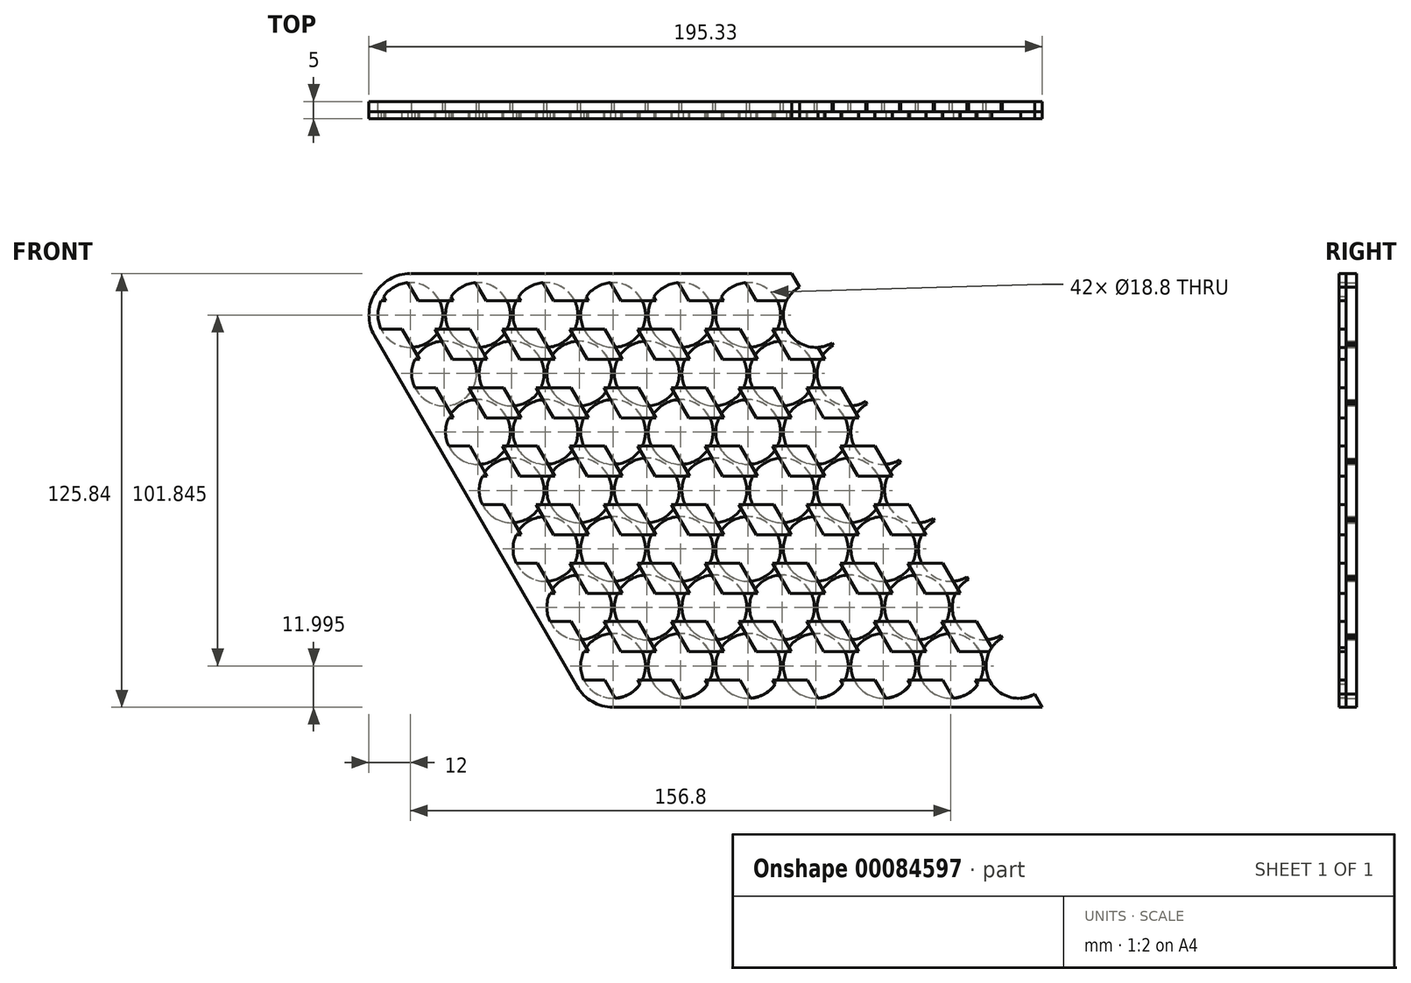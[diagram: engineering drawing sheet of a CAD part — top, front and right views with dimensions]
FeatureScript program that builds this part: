
annotation { "Feature Type Name" : "Feature", "Feature Type Description" : "" }
export const myFeature = defineFeature(function(context is Context, id is Id, definition is map)
    precondition{}
    {
        {
            var Q0;
            Q0=qCreatedBy(makeId("Front.planeOp"),FACE);
            var sketch = newSketch(context, id + "F0", { "sketchPlane" : qUnion([Q0]) });
            skLineSegment(sketch, "E0", {"start": v(0, 0) * mm, "end": v(79.44, 0) * mm, "construction": true});
            skLineSegment(sketch, "E1", {"start": v(0, 0) * mm, "end": v(43.4, -75.16) * mm, "construction": true});
            skCircle(sketch, "E2", {"center": v(0, 0) * mm, "radius": 9.4 * mm});
            skCircle(sketch, "E3.1.0.0", {"center": v(19.6, 0) * mm, "radius": 9.4 * mm});
            skCircle(sketch, "E3.2.0.0", {"center": v(39.2, 0) * mm, "radius": 9.4 * mm});
            skCircle(sketch, "E3.3.0.0", {"center": v(58.8, 0) * mm, "radius": 9.4 * mm});
            skCircle(sketch, "E3.4.0.0", {"center": v(78.4, 0) * mm, "radius": 9.4 * mm});
            skCircle(sketch, "E3.5.0.0", {"center": v(98, 0) * mm, "radius": 9.4 * mm});
            skArc(sketch, "E3.6.0.0", {"start": v(112.9, 8.14) * mm, "mid": v(109.46, -4.7) * mm, "end": v(122.3, -8.14) * mm});
            skLineSegment(sketch, "E3.direction1", {"start": v(0, 0) * mm, "end": v(19.6, 0) * mm, "construction": true});
            skCircle(sketch, "E4.1.0.0", {"center": v(9.8, -16.97) * mm, "radius": 9.4 * mm});
            skCircle(sketch, "E4.2.0.0", {"center": v(19.6, -33.95) * mm, "radius": 9.4 * mm});
            skCircle(sketch, "E4.3.0.0", {"center": v(29.4, -50.92) * mm, "radius": 9.4 * mm});
            skCircle(sketch, "E4.4.0.0", {"center": v(39.2, -67.9) * mm, "radius": 9.4 * mm});
            skCircle(sketch, "E4.5.0.0", {"center": v(49, -84.87) * mm, "radius": 9.4 * mm});
            skCircle(sketch, "E4.6.0.0", {"center": v(58.8, -101.84) * mm, "radius": 9.4 * mm});
            skLineSegment(sketch, "E4.direction1", {"start": v(0, 0) * mm, "end": v(9.8, -16.97) * mm, "construction": true});
            skCircle(sketch, "E5.1.0.0", {"center": v(29.4, -16.97) * mm, "radius": 9.4 * mm});
            skCircle(sketch, "E5.1.0.1", {"center": v(39.2, -33.95) * mm, "radius": 9.4 * mm});
            skCircle(sketch, "E5.1.0.2", {"center": v(49, -50.92) * mm, "radius": 9.4 * mm});
            skCircle(sketch, "E5.1.0.3", {"center": v(58.8, -67.9) * mm, "radius": 9.4 * mm});
            skCircle(sketch, "E5.1.0.4", {"center": v(68.6, -84.87) * mm, "radius": 9.4 * mm});
            skCircle(sketch, "E5.1.0.5", {"center": v(78.4, -101.84) * mm, "radius": 9.4 * mm});
            skCircle(sketch, "E5.2.0.0", {"center": v(49, -16.97) * mm, "radius": 9.4 * mm});
            skCircle(sketch, "E5.2.0.1", {"center": v(58.8, -33.95) * mm, "radius": 9.4 * mm});
            skCircle(sketch, "E5.2.0.2", {"center": v(68.6, -50.92) * mm, "radius": 9.4 * mm});
            skCircle(sketch, "E5.2.0.3", {"center": v(78.4, -67.9) * mm, "radius": 9.4 * mm});
            skCircle(sketch, "E5.2.0.4", {"center": v(88.2, -84.87) * mm, "radius": 9.4 * mm});
            skCircle(sketch, "E5.2.0.5", {"center": v(98, -101.84) * mm, "radius": 9.4 * mm});
            skCircle(sketch, "E5.3.0.0", {"center": v(68.6, -16.97) * mm, "radius": 9.4 * mm});
            skCircle(sketch, "E5.3.0.1", {"center": v(78.4, -33.95) * mm, "radius": 9.4 * mm});
            skCircle(sketch, "E5.3.0.2", {"center": v(88.2, -50.92) * mm, "radius": 9.4 * mm});
            skCircle(sketch, "E5.3.0.3", {"center": v(98, -67.9) * mm, "radius": 9.4 * mm});
            skCircle(sketch, "E5.3.0.4", {"center": v(107.8, -84.87) * mm, "radius": 9.4 * mm});
            skCircle(sketch, "E5.3.0.5", {"center": v(117.6, -101.84) * mm, "radius": 9.4 * mm});
            skCircle(sketch, "E5.4.0.0", {"center": v(88.2, -16.97) * mm, "radius": 9.4 * mm});
            skCircle(sketch, "E5.4.0.1", {"center": v(98, -33.95) * mm, "radius": 9.4 * mm});
            skCircle(sketch, "E5.4.0.2", {"center": v(107.8, -50.92) * mm, "radius": 9.4 * mm});
            skCircle(sketch, "E5.4.0.3", {"center": v(117.6, -67.9) * mm, "radius": 9.4 * mm});
            skCircle(sketch, "E5.4.0.4", {"center": v(127.4, -84.87) * mm, "radius": 9.4 * mm});
            skCircle(sketch, "E5.4.0.5", {"center": v(137.2, -101.84) * mm, "radius": 9.4 * mm});
            skCircle(sketch, "E5.5.0.0", {"center": v(107.8, -16.97) * mm, "radius": 9.4 * mm});
            skCircle(sketch, "E5.5.0.1", {"center": v(117.6, -33.95) * mm, "radius": 9.4 * mm});
            skCircle(sketch, "E5.5.0.2", {"center": v(127.4, -50.92) * mm, "radius": 9.4 * mm});
            skCircle(sketch, "E5.5.0.3", {"center": v(137.2, -67.9) * mm, "radius": 9.4 * mm});
            skCircle(sketch, "E5.5.0.4", {"center": v(147, -84.87) * mm, "radius": 9.4 * mm});
            skCircle(sketch, "E5.5.0.5", {"center": v(156.8, -101.84) * mm, "radius": 9.4 * mm});
            skArc(sketch, "E5.6.0.0", {"start": v(122.7, -8.83) * mm, "mid": v(119.26, -21.67) * mm, "end": v(132.1, -25.11) * mm});
            skArc(sketch, "E5.6.0.1", {"start": v(132.5, -25.8) * mm, "mid": v(129.06, -38.65) * mm, "end": v(141.9, -42.09) * mm});
            skArc(sketch, "E5.6.0.2", {"start": v(142.3, -42.78) * mm, "mid": v(138.86, -55.62) * mm, "end": v(151.7, -59.06) * mm});
            skArc(sketch, "E5.6.0.3", {"start": v(152.1, -59.76) * mm, "mid": v(148.66, -72.6) * mm, "end": v(161.5, -76.04) * mm});
            skArc(sketch, "E5.6.0.4", {"start": v(161.9, -76.73) * mm, "mid": v(158.46, -89.57) * mm, "end": v(171.3, -93.01) * mm});
            skArc(sketch, "E5.6.0.5", {"start": v(171.7, -93.7) * mm, "mid": v(168.26, -106.54) * mm, "end": v(181.1, -109.99) * mm});
            skLineSegment(sketch, "E5.direction1", {"start": v(9.8, -16.97) * mm, "end": v(29.4, -16.97) * mm, "construction": true});
            skLineSegment(sketch, "E6", {"start": v(0, 0) * mm, "end": v(127, 0) * mm, "construction": true});
            skLineSegment(sketch, "E7", {"start": v(441, -118.82) * mm, "end": v(68.6, -118.82) * mm, "construction": true});
            skLineSegment(sketch, "E8", {"start": v(68.6, -118.82) * mm, "end": v(0, 0) * mm, "construction": true});
            skArc(sketch, "E9", {"start": v(48.4, -107.84) * mm, "mid": v(52.8, -112.24) * mm, "end": v(58.8, -113.84) * mm});
            skArc(sketch, "E10", {"start": v(0, 12) * mm, "mid": v(-10.4, 6) * mm, "end": v(-10.4, -6) * mm});
            skLineSegment(sketch, "E11", {"start": v(0, 12) * mm, "end": v(110.67, 12) * mm});
            skLineSegment(sketch, "E12", {"start": v(-10.4, -6) * mm, "end": v(48.4, -107.84) * mm});
            skLineSegment(sketch, "E13", {"start": v(58.8, -113.84) * mm, "end": v(183.33, -113.84) * mm});
            skLineSegment(sketch, "E14", {"start": v(117.6, 0) * mm, "end": v(176.4, -101.84) * mm});
            skLineSegment(sketch, "E15", {"start": v(176.4, -101.84) * mm, "end": v(183.33, -113.84) * mm});
            skLineSegment(sketch, "E16", {"start": v(117.6, 0) * mm, "end": v(110.67, 12) * mm});
            skSolve(sketch);
        }
        {
            var Q0;
            Q0=makeQuery(id+"F0.imprint","IMPRINT",FACE,{"disambiguationData":[TD([[makeQuery(id+"F0.imprint","IMPRINT",EDGE,{"derivedFrom":sQuery(id+"F0.wireOp",EDGE,"E2")}),-1.0]])]});
            extrude(context, id + "F1", {"entities" : qUnion([Q0]), "depth" : 3 * mm});
        }
        {
            var Q0;
            Q0=makeQuery(id+"F1.opExtrude","CAP_FACE",FACE,{"disambiguationData":[OSD([sQuery(id+"F0.wireOp",EDGE,"E2"),sQuery(id+"F0.wireOp",EDGE,"E3.1.0.0"),sQuery(id+"F0.wireOp",EDGE,"E3.2.0.0"),sQuery(id+"F0.wireOp",EDGE,"E3.3.0.0"),sQuery(id+"F0.wireOp",EDGE,"E3.4.0.0"),sQuery(id+"F0.wireOp",EDGE,"E3.5.0.0"),sQuery(id+"F0.wireOp",EDGE,"E3.6.0.0"),sQuery(id+"F0.wireOp",EDGE,"E3.7.0.0"),sQuery(id+"F0.wireOp",EDGE,"E3.8.0.0"),sQuery(id+"F0.wireOp",EDGE,"E3.9.0.0"),sQuery(id+"F0.wireOp",EDGE,"E3.10.0.0"),sQuery(id+"F0.wireOp",EDGE,"E3.11.0.0"),sQuery(id+"F0.wireOp",EDGE,"E3.12.0.0"),sQuery(id+"F0.wireOp",EDGE,"E3.13.0.0"),sQuery(id+"F0.wireOp",EDGE,"E3.14.0.0"),sQuery(id+"F0.wireOp",EDGE,"E3.15.0.0"),sQuery(id+"F0.wireOp",EDGE,"E3.16.0.0"),sQuery(id+"F0.wireOp",EDGE,"E3.17.0.0"),sQuery(id+"F0.wireOp",EDGE,"E3.18.0.0"),sQuery(id+"F0.wireOp",EDGE,"E3.19.0.0"),sQuery(id+"F0.wireOp",EDGE,"E4.1.0.0"),sQuery(id+"F0.wireOp",EDGE,"E4.2.0.0"),sQuery(id+"F0.wireOp",EDGE,"E4.3.0.0"),sQuery(id+"F0.wireOp",EDGE,"E4.4.0.0"),sQuery(id+"F0.wireOp",EDGE,"E4.5.0.0"),sQuery(id+"F0.wireOp",EDGE,"E4.6.0.0"),sQuery(id+"F0.wireOp",EDGE,"E5.1.0.0"),sQuery(id+"F0.wireOp",EDGE,"E5.1.0.1"),sQuery(id+"F0.wireOp",EDGE,"E5.1.0.2"),sQuery(id+"F0.wireOp",EDGE,"E5.1.0.3"),sQuery(id+"F0.wireOp",EDGE,"E5.1.0.4"),sQuery(id+"F0.wireOp",EDGE,"E5.1.0.5"),sQuery(id+"F0.wireOp",EDGE,"E5.2.0.0"),sQuery(id+"F0.wireOp",EDGE,"E5.2.0.1"),sQuery(id+"F0.wireOp",EDGE,"E5.2.0.2"),sQuery(id+"F0.wireOp",EDGE,"E5.2.0.3"),sQuery(id+"F0.wireOp",EDGE,"E5.2.0.4"),sQuery(id+"F0.wireOp",EDGE,"E5.2.0.5"),sQuery(id+"F0.wireOp",EDGE,"E5.3.0.0"),sQuery(id+"F0.wireOp",EDGE,"E5.3.0.1"),sQuery(id+"F0.wireOp",EDGE,"E5.3.0.2"),sQuery(id+"F0.wireOp",EDGE,"E5.3.0.3"),sQuery(id+"F0.wireOp",EDGE,"E5.3.0.4"),sQuery(id+"F0.wireOp",EDGE,"E5.3.0.5"),sQuery(id+"F0.wireOp",EDGE,"E5.4.0.0"),sQuery(id+"F0.wireOp",EDGE,"E5.4.0.1"),sQuery(id+"F0.wireOp",EDGE,"E5.4.0.2"),sQuery(id+"F0.wireOp",EDGE,"E5.4.0.3"),sQuery(id+"F0.wireOp",EDGE,"E5.4.0.4"),sQuery(id+"F0.wireOp",EDGE,"E5.4.0.5"),sQuery(id+"F0.wireOp",EDGE,"E5.5.0.0"),sQuery(id+"F0.wireOp",EDGE,"E5.5.0.1"),sQuery(id+"F0.wireOp",EDGE,"E5.5.0.2"),sQuery(id+"F0.wireOp",EDGE,"E5.5.0.3"),sQuery(id+"F0.wireOp",EDGE,"E5.5.0.4"),sQuery(id+"F0.wireOp",EDGE,"E5.5.0.5"),sQuery(id+"F0.wireOp",EDGE,"E5.6.0.0"),sQuery(id+"F0.wireOp",EDGE,"E5.6.0.1"),sQuery(id+"F0.wireOp",EDGE,"E5.6.0.2"),sQuery(id+"F0.wireOp",EDGE,"E5.6.0.3"),sQuery(id+"F0.wireOp",EDGE,"E5.6.0.4"),sQuery(id+"F0.wireOp",EDGE,"E5.6.0.5"),sQuery(id+"F0.wireOp",EDGE,"E5.7.0.0"),sQuery(id+"F0.wireOp",EDGE,"E5.7.0.1"),sQuery(id+"F0.wireOp",EDGE,"E5.7.0.2"),sQuery(id+"F0.wireOp",EDGE,"E5.7.0.3"),sQuery(id+"F0.wireOp",EDGE,"E5.7.0.4"),sQuery(id+"F0.wireOp",EDGE,"E5.7.0.5"),sQuery(id+"F0.wireOp",EDGE,"E5.8.0.0"),sQuery(id+"F0.wireOp",EDGE,"E5.8.0.1"),sQuery(id+"F0.wireOp",EDGE,"E5.8.0.2"),sQuery(id+"F0.wireOp",EDGE,"E5.8.0.3"),sQuery(id+"F0.wireOp",EDGE,"E5.8.0.4"),sQuery(id+"F0.wireOp",EDGE,"E5.8.0.5"),sQuery(id+"F0.wireOp",EDGE,"E5.9.0.0"),sQuery(id+"F0.wireOp",EDGE,"E5.9.0.1"),sQuery(id+"F0.wireOp",EDGE,"E5.9.0.2"),sQuery(id+"F0.wireOp",EDGE,"E5.9.0.3"),sQuery(id+"F0.wireOp",EDGE,"E5.9.0.4"),sQuery(id+"F0.wireOp",EDGE,"E5.9.0.5"),sQuery(id+"F0.wireOp",EDGE,"E5.10.0.0"),sQuery(id+"F0.wireOp",EDGE,"E5.10.0.1"),sQuery(id+"F0.wireOp",EDGE,"E5.10.0.2"),sQuery(id+"F0.wireOp",EDGE,"E5.10.0.3"),sQuery(id+"F0.wireOp",EDGE,"E5.10.0.4"),sQuery(id+"F0.wireOp",EDGE,"E5.10.0.5"),sQuery(id+"F0.wireOp",EDGE,"E5.11.0.0"),sQuery(id+"F0.wireOp",EDGE,"E5.11.0.1"),sQuery(id+"F0.wireOp",EDGE,"E5.11.0.2"),sQuery(id+"F0.wireOp",EDGE,"E5.11.0.3"),sQuery(id+"F0.wireOp",EDGE,"E5.11.0.4"),sQuery(id+"F0.wireOp",EDGE,"E5.11.0.5"),sQuery(id+"F0.wireOp",EDGE,"E5.12.0.0"),sQuery(id+"F0.wireOp",EDGE,"E5.12.0.1"),sQuery(id+"F0.wireOp",EDGE,"E5.12.0.2"),sQuery(id+"F0.wireOp",EDGE,"E5.12.0.3"),sQuery(id+"F0.wireOp",EDGE,"E5.12.0.4"),sQuery(id+"F0.wireOp",EDGE,"E5.12.0.5"),sQuery(id+"F0.wireOp",EDGE,"E5.13.0.0"),sQuery(id+"F0.wireOp",EDGE,"E5.13.0.1"),sQuery(id+"F0.wireOp",EDGE,"E5.13.0.2"),sQuery(id+"F0.wireOp",EDGE,"E5.13.0.3"),sQuery(id+"F0.wireOp",EDGE,"E5.13.0.4"),sQuery(id+"F0.wireOp",EDGE,"E5.13.0.5"),sQuery(id+"F0.wireOp",EDGE,"E5.14.0.0"),sQuery(id+"F0.wireOp",EDGE,"E5.14.0.1"),sQuery(id+"F0.wireOp",EDGE,"E5.14.0.2"),sQuery(id+"F0.wireOp",EDGE,"E5.14.0.3"),sQuery(id+"F0.wireOp",EDGE,"E5.14.0.4"),sQuery(id+"F0.wireOp",EDGE,"E5.14.0.5"),sQuery(id+"F0.wireOp",EDGE,"E5.15.0.0"),sQuery(id+"F0.wireOp",EDGE,"E5.15.0.1"),sQuery(id+"F0.wireOp",EDGE,"E5.15.0.2"),sQuery(id+"F0.wireOp",EDGE,"E5.15.0.3"),sQuery(id+"F0.wireOp",EDGE,"E5.15.0.4"),sQuery(id+"F0.wireOp",EDGE,"E5.15.0.5"),sQuery(id+"F0.wireOp",EDGE,"E5.16.0.0"),sQuery(id+"F0.wireOp",EDGE,"E5.16.0.1"),sQuery(id+"F0.wireOp",EDGE,"E5.16.0.2"),sQuery(id+"F0.wireOp",EDGE,"E5.16.0.3"),sQuery(id+"F0.wireOp",EDGE,"E5.16.0.4"),sQuery(id+"F0.wireOp",EDGE,"E5.16.0.5"),sQuery(id+"F0.wireOp",EDGE,"E5.17.0.0"),sQuery(id+"F0.wireOp",EDGE,"E5.17.0.1"),sQuery(id+"F0.wireOp",EDGE,"E5.17.0.2"),sQuery(id+"F0.wireOp",EDGE,"E5.17.0.3"),sQuery(id+"F0.wireOp",EDGE,"E5.17.0.4"),sQuery(id+"F0.wireOp",EDGE,"E5.17.0.5"),sQuery(id+"F0.wireOp",EDGE,"E5.18.0.0"),sQuery(id+"F0.wireOp",EDGE,"E5.18.0.1"),sQuery(id+"F0.wireOp",EDGE,"E5.18.0.2"),sQuery(id+"F0.wireOp",EDGE,"E5.18.0.3"),sQuery(id+"F0.wireOp",EDGE,"E5.18.0.4"),sQuery(id+"F0.wireOp",EDGE,"E5.18.0.5"),sQuery(id+"F0.wireOp",EDGE,"E5.19.0.0"),sQuery(id+"F0.wireOp",EDGE,"E5.19.0.1"),sQuery(id+"F0.wireOp",EDGE,"E5.19.0.2"),sQuery(id+"F0.wireOp",EDGE,"E5.19.0.3"),sQuery(id+"F0.wireOp",EDGE,"E5.19.0.4"),sQuery(id+"F0.wireOp",EDGE,"E5.19.0.5"),sQuery(id+"F0.wireOp",EDGE,"E9"),sQuery(id+"F0.wireOp",EDGE,"5nUdW9fS-2cd6-qMiR-XE9V-vxUMlnSNgniM"),sQuery(id+"F0.wireOp",EDGE,"tvQ31exZ-RF6j-dpE3-HDwJ-fjnaVMTG8jao"),sQuery(id+"F0.wireOp",EDGE,"E10"),sQuery(id+"F0.wireOp",EDGE,"E11"),sQuery(id+"F0.wireOp",EDGE,"E12"),sQuery(id+"F0.wireOp",EDGE,"E13"),sQuery(id+"F0.wireOp",EDGE,"rU4Kxbuf-INRG-fgL3-azAB-AAWa3zM6NOq8")])],"isStart":false});
            var sketch = newSketch(context, id + "F2", { "sketchPlane" : qUnion([Q0]) });
            skLineSegment(sketch, "E17.0", {"start": v(0, 12) * mm, "end": v(110.67, 12) * mm});
            skArc(sketch, "E17.1", {"start": v(0, 12) * mm, "mid": v(-10.4, 6) * mm, "end": v(-10.4, -6) * mm});
            skLineSegment(sketch, "E17.2", {"start": v(-10.4, -6) * mm, "end": v(48.4, -107.84) * mm});
            skLineSegment(sketch, "E17.6", {"start": v(58.8, -113.84) * mm, "end": v(183.33, -113.84) * mm});
            skArc(sketch, "E17.7", {"start": v(48.4, -107.84) * mm, "mid": v(52.8, -112.24) * mm, "end": v(58.8, -113.84) * mm});
            skLineSegment(sketch, "E18", {"start": v(117.6, 0) * mm, "end": v(176.4, -101.84) * mm});
            skLineSegment(sketch, "E19", {"start": v(117.6, 0) * mm, "end": v(110.67, 12) * mm});
            skLineSegment(sketch, "E20", {"start": v(176.4, -101.84) * mm, "end": v(183.33, -113.84) * mm});
            skPoint(sketch, "E17.3.end.orphan", {"position": v(0, 12) * mm});
            skSolve(sketch);
        }
        {
            var Q0;
            Q0=qSketchRegion(id+"F2",true);
            extrude(context, id + "F3", {"entities" : qUnion([Q0]), "depth" : 2 * mm});
        }
        {
            var Q0;
            Q0=makeQuery(id+"F3.opExtrude","CAP_FACE",FACE,{"disambiguationData":[OSD([sQuery(id+"F2.wireOp",EDGE,"E17.0"),sQuery(id+"F2.wireOp",EDGE,"E17.1"),sQuery(id+"F2.wireOp",EDGE,"E17.2"),sQuery(id+"F2.wireOp",EDGE,"E17.3"),sQuery(id+"F2.wireOp",EDGE,"E17.4"),sQuery(id+"F2.wireOp",EDGE,"E17.5"),sQuery(id+"F2.wireOp",EDGE,"E17.6"),sQuery(id+"F2.wireOp",EDGE,"E17.7")])],"isStart":false});
            var sketch = newSketch(context, id + "F4", { "sketchPlane" : qUnion([Q0]) });
            skLineSegment(sketch, "E21", {"start": v(0, 0) * mm, "end": v(58.8, -101.84) * mm, "construction": true});
            skLineSegment(sketch, "E22", {"start": v(58.8, -101.84) * mm, "end": v(176.4, -101.84) * mm, "construction": true});
            skLineSegment(sketch, "E23", {"start": v(117.6, 0) * mm, "end": v(0, 0) * mm, "construction": true});
            skLineSegment(sketch, "E24", {"start": v(-8.46, 4.1) * mm, "end": v(115.23, 4.1) * mm});
            skLineSegment(sketch, "E25.MirrorCS", {"start": v(-8.46, -4.1) * mm, "end": v(119.97, -4.1) * mm});
            skArc(sketch, "E26.0", {"start": v(-8.46, 4.1) * mm, "mid": v(-9.4, 0) * mm, "end": v(-8.46, -4.1) * mm});
            skPoint(sketch, "E27.orphan", {"position": v(-44.99, 4.1) * mm});
            skPoint(sketch, "E28.orphan", {"position": v(-44.99, -4.1) * mm});
            skLineSegment(sketch, "E29.0.1.0", {"start": v(1.34, -12.87) * mm, "end": v(125.03, -12.87) * mm});
            skLineSegment(sketch, "E29.0.1.1", {"start": v(1.34, -21.07) * mm, "end": v(129.77, -21.07) * mm});
            skArc(sketch, "E29.0.1.2", {"start": v(1.34, -12.87) * mm, "mid": v(0.4, -16.97) * mm, "end": v(1.34, -21.07) * mm});
            skLineSegment(sketch, "E29.0.2.0", {"start": v(11.14, -29.85) * mm, "end": v(134.83, -29.85) * mm});
            skLineSegment(sketch, "E29.0.2.1", {"start": v(11.14, -38.05) * mm, "end": v(139.57, -38.05) * mm});
            skArc(sketch, "E29.0.2.2", {"start": v(11.14, -29.85) * mm, "mid": v(10.2, -33.95) * mm, "end": v(11.14, -38.05) * mm});
            skLineSegment(sketch, "E29.0.3.0", {"start": v(20.94, -46.82) * mm, "end": v(144.63, -46.82) * mm});
            skLineSegment(sketch, "E29.0.3.1", {"start": v(20.94, -55.02) * mm, "end": v(149.37, -55.02) * mm});
            skArc(sketch, "E29.0.3.2", {"start": v(20.94, -46.82) * mm, "mid": v(20, -50.92) * mm, "end": v(20.94, -55.02) * mm});
            skLineSegment(sketch, "E29.0.4.0", {"start": v(30.74, -63.8) * mm, "end": v(154.43, -63.8) * mm});
            skLineSegment(sketch, "E29.0.4.1", {"start": v(30.74, -72) * mm, "end": v(159.17, -72) * mm});
            skArc(sketch, "E29.0.4.2", {"start": v(30.74, -63.8) * mm, "mid": v(29.8, -67.9) * mm, "end": v(30.74, -72) * mm});
            skLineSegment(sketch, "E29.0.5.0", {"start": v(40.54, -80.77) * mm, "end": v(164.23, -80.77) * mm});
            skLineSegment(sketch, "E29.0.5.1", {"start": v(40.54, -88.97) * mm, "end": v(168.97, -88.97) * mm});
            skArc(sketch, "E29.0.5.2", {"start": v(40.54, -80.77) * mm, "mid": v(39.6, -84.87) * mm, "end": v(40.54, -88.97) * mm});
            skLineSegment(sketch, "E29.0.6.0", {"start": v(50.34, -97.74) * mm, "end": v(174.03, -97.74) * mm});
            skLineSegment(sketch, "E29.0.6.1", {"start": v(50.34, -105.94) * mm, "end": v(178.77, -105.94) * mm});
            skArc(sketch, "E29.0.6.2", {"start": v(50.34, -97.74) * mm, "mid": v(49.4, -101.84) * mm, "end": v(50.34, -105.94) * mm});
            skLineSegment(sketch, "E29.direction1", {"start": v(-8.46, 4.1) * mm, "end": v(16.54, 4.1) * mm, "construction": true});
            skLineSegment(sketch, "E29.direction2", {"start": v(-8.46, 4.1) * mm, "end": v(1.34, -12.87) * mm, "construction": true});
            skArc(sketch, "E30.0", {"start": v(171.7, -93.7) * mm, "mid": v(168.26, -106.54) * mm, "end": v(181.1, -109.99) * mm});
            skArc(sketch, "E31.0", {"start": v(112.9, 8.14) * mm, "mid": v(109.46, -4.7) * mm, "end": v(122.3, -8.14) * mm});
            skLineSegment(sketch, "E32", {"start": v(176.4, -101.84) * mm, "end": v(117.6, 0) * mm});
            skLineSegment(sketch, "E33", {"start": v(176.4, -101.84) * mm, "end": v(190.68, -126.58) * mm});
            skLineSegment(sketch, "E34", {"start": v(117.6, 0) * mm, "end": v(104.13, 23.33) * mm});
            skPoint(sketch, "E35.orphan", {"position": v(185.8, -101.84) * mm});
            skSolve(sketch);
        }
        {
            var Q0;
            Q0=qSketchRegion(id+"F4",true);
            extrude(context, id + "F5", {"entities" : qUnion([Q0]), "operationType" : NewBodyOperationType.REMOVE, "endBound" : BoundingType.UP_TO_NEXT, "oppositeDirection" : true, "depth" : 25 * mm});
        }
        {
            var Q0;
            Q0=makeQuery(id+"F3.opExtrude","CAP_FACE",FACE,{"disambiguationData":[OSD([sQuery(id+"F2.wireOp",EDGE,"E17.0"),sQuery(id+"F2.wireOp",EDGE,"E17.1"),sQuery(id+"F2.wireOp",EDGE,"E17.2"),sQuery(id+"F2.wireOp",EDGE,"E17.3"),sQuery(id+"F2.wireOp",EDGE,"E17.4"),sQuery(id+"F2.wireOp",EDGE,"E17.5"),sQuery(id+"F2.wireOp",EDGE,"E17.6"),sQuery(id+"F2.wireOp",EDGE,"E17.7")])],"isStart":false});
            var sketch = newSketch(context, id + "F6", { "sketchPlane" : qUnion([Q0]) });
            skLineSegment(sketch, "E36", {"start": v(0, 0) * mm, "end": v(58.8, -101.84) * mm, "construction": true});
            skLineSegment(sketch, "E37", {"start": v(-0.68, 9.38) * mm, "end": v(66.63, -107.21) * mm});
            skLineSegment(sketch, "E38.MirrorCS", {"start": v(-7.78, 5.28) * mm, "end": v(59.5, -111.26) * mm});
            skArc(sketch, "E39.0", {"start": v(-0.68, 9.38) * mm, "mid": v(-4.7, 8.14) * mm, "end": v(-7.78, 5.28) * mm});
            skArc(sketch, "E40.trimOffspring", {"start": v(59.5, -111.26) * mm, "mid": v(63.53, -110.05) * mm, "end": v(66.63, -107.21) * mm});
            skPoint(sketch, "E41.orphan", {"position": v(72.04, -132.98) * mm});
            skPoint(sketch, "E42.orphan", {"position": v(79.14, -128.88) * mm});
            skPoint(sketch, "E43.orphan", {"position": v(-6.6, 19.64) * mm});
            skPoint(sketch, "E44.orphan", {"position": v(-13.7, 15.54) * mm});
            skArc(sketch, "E45.1.0.0", {"start": v(18.92, 9.38) * mm, "mid": v(14.9, 8.14) * mm, "end": v(11.82, 5.28) * mm});
            skLineSegment(sketch, "E45.1.0.1", {"start": v(11.82, 5.28) * mm, "end": v(79.1, -111.26) * mm});
            skLineSegment(sketch, "E45.1.0.2", {"start": v(18.92, 9.38) * mm, "end": v(86.23, -107.21) * mm});
            skArc(sketch, "E45.1.0.3", {"start": v(79.1, -111.26) * mm, "mid": v(83.13, -110.05) * mm, "end": v(86.23, -107.21) * mm});
            skArc(sketch, "E45.2.0.0", {"start": v(38.52, 9.38) * mm, "mid": v(34.5, 8.14) * mm, "end": v(31.42, 5.28) * mm});
            skLineSegment(sketch, "E45.2.0.1", {"start": v(31.42, 5.28) * mm, "end": v(98.7, -111.26) * mm});
            skLineSegment(sketch, "E45.2.0.2", {"start": v(38.52, 9.38) * mm, "end": v(105.83, -107.21) * mm});
            skArc(sketch, "E45.2.0.3", {"start": v(98.7, -111.26) * mm, "mid": v(102.73, -110.05) * mm, "end": v(105.83, -107.21) * mm});
            skArc(sketch, "E45.3.0.0", {"start": v(58.12, 9.38) * mm, "mid": v(54.1, 8.14) * mm, "end": v(51.02, 5.28) * mm});
            skLineSegment(sketch, "E45.3.0.1", {"start": v(51.02, 5.28) * mm, "end": v(118.3, -111.26) * mm});
            skLineSegment(sketch, "E45.3.0.2", {"start": v(58.12, 9.38) * mm, "end": v(125.43, -107.21) * mm});
            skArc(sketch, "E45.3.0.3", {"start": v(118.3, -111.26) * mm, "mid": v(122.33, -110.05) * mm, "end": v(125.43, -107.21) * mm});
            skArc(sketch, "E45.4.0.0", {"start": v(77.72, 9.38) * mm, "mid": v(73.7, 8.14) * mm, "end": v(70.62, 5.28) * mm});
            skLineSegment(sketch, "E45.4.0.1", {"start": v(70.62, 5.28) * mm, "end": v(137.9, -111.26) * mm});
            skLineSegment(sketch, "E45.4.0.2", {"start": v(77.72, 9.38) * mm, "end": v(145.03, -107.21) * mm});
            skArc(sketch, "E45.4.0.3", {"start": v(137.9, -111.26) * mm, "mid": v(141.93, -110.05) * mm, "end": v(145.03, -107.21) * mm});
            skArc(sketch, "E45.5.0.0", {"start": v(97.32, 9.38) * mm, "mid": v(93.3, 8.14) * mm, "end": v(90.22, 5.28) * mm});
            skLineSegment(sketch, "E45.5.0.1", {"start": v(90.22, 5.28) * mm, "end": v(157.5, -111.26) * mm});
            skLineSegment(sketch, "E45.5.0.2", {"start": v(97.32, 9.38) * mm, "end": v(164.63, -107.21) * mm});
            skArc(sketch, "E45.5.0.3", {"start": v(157.5, -111.26) * mm, "mid": v(161.53, -110.05) * mm, "end": v(164.63, -107.21) * mm});
            skArc(sketch, "E45.6.0.0", {"start": v(116.92, 9.38) * mm, "mid": v(112.9, 8.14) * mm, "end": v(109.82, 5.28) * mm});
            skLineSegment(sketch, "E45.6.0.1", {"start": v(109.82, 5.28) * mm, "end": v(177.1, -111.26) * mm});
            skArc(sketch, "E45.6.0.3", {"start": v(177.1, -111.26) * mm, "mid": v(181.13, -110.05) * mm, "end": v(184.23, -107.21) * mm});
            skLineSegment(sketch, "E45.direction1", {"start": v(-7.78, 5.28) * mm, "end": v(11.82, 5.28) * mm, "construction": true});
            skLineSegment(sketch, "E46", {"start": v(117.6, 0) * mm, "end": v(198.51, -140.14) * mm, "construction": true});
            skLineSegment(sketch, "E47", {"start": v(117.6, 0) * mm, "end": v(96.58, 36.42) * mm, "construction": true});
            skLineSegment(sketch, "E48", {"start": v(116.92, 9.38) * mm, "end": v(184.23, -107.21) * mm});
            skSolve(sketch);
        }
        {
            var Q0;
            Q0=qSketchRegion(id+"F6",true);
            extrude(context, id + "F7", {"entities" : qUnion([Q0]), "operationType" : NewBodyOperationType.REMOVE, "oppositeDirection" : true, "depth" : 2 * mm});
        }
    });
